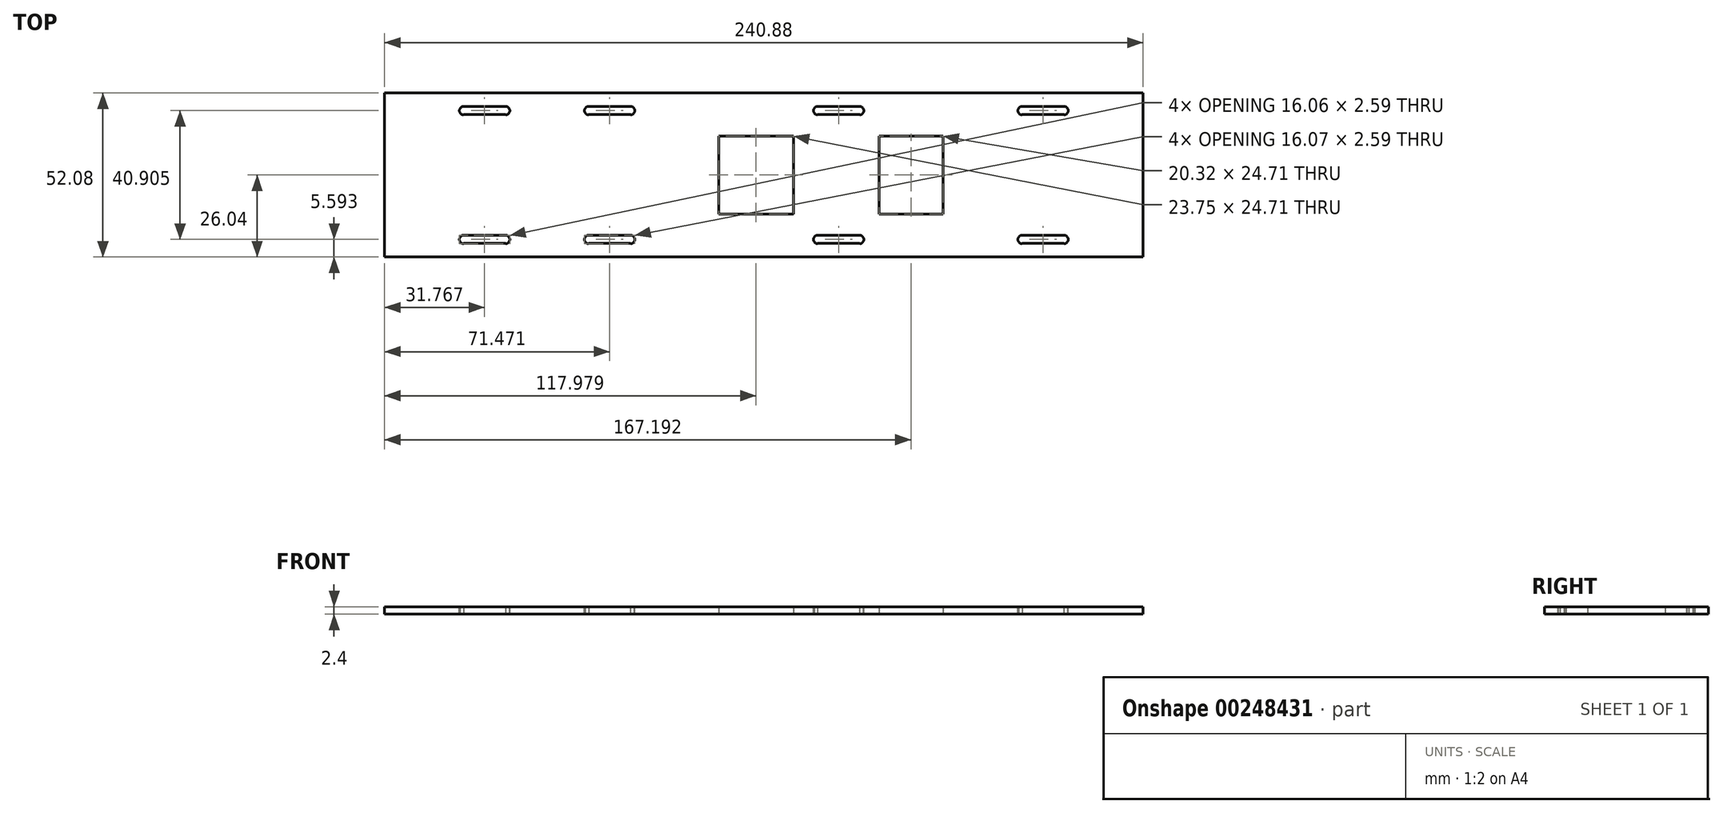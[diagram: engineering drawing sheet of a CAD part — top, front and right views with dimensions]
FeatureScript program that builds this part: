
annotation { "Feature Type Name" : "Feature", "Feature Type Description" : "" }
export const myFeature = defineFeature(function(context is Context, id is Id, definition is map)
    precondition{}
    {
        {
            var Q0;
            Q0=qCreatedBy(makeId("Top.planeOp"),FACE);
            var sketch = newSketch(context, id + "F0", { "sketchPlane" : qUnion([Q0])});
            skLineSegment(sketch, "E0", {"start": v(120.44, 26.04) * mm, "end": v(120.44, -26.04) * mm});
            skLineSegment(sketch, "E1", {"start": v(120.44, -26.04) * mm, "end": v(-120.44, -26.04) * mm});
            skLineSegment(sketch, "E2", {"start": v(-120.44, -26.04) * mm, "end": v(-120.44, 26.04) * mm});
            skLineSegment(sketch, "E3", {"start": v(-120.44, 26.04) * mm, "end": v(120.44, 26.04) * mm});
            skLineSegment(sketch, "E4", {"start": v(-95.34, -19.17) * mm, "end": v(-82.02, -19.17) * mm});
            skFitSpline(sketch, "E5", {"points": [v(-95.33, -19.17) * mm, v(-95.79, -19.17) * mm, v(-96.2, -19.41) * mm, v(-96.44, -19.8) * mm]});
            skFitSpline(sketch, "E6", {"points": [v(-96.44, -19.8) * mm, v(-96.67, -20.2) * mm, v(-96.67, -20.7) * mm, v(-96.44, -21.09) * mm]});
            skFitSpline(sketch, "E7", {"points": [v(-96.44, -21.09) * mm, v(-96.2, -21.48) * mm, v(-95.79, -21.72) * mm, v(-95.33, -21.72) * mm]});
            skFitSpline(sketch, "E8", {"points": [v(-82.02, -21.72) * mm, v(-81.56, -21.72) * mm, v(-81.14, -21.48) * mm, v(-80.9, -21.09) * mm]});
            skFitSpline(sketch, "E9", {"points": [v(-80.9, -21.09) * mm, v(-80.68, -20.7) * mm, v(-80.68, -20.2) * mm, v(-80.9, -19.8) * mm]});
            skFitSpline(sketch, "E10", {"points": [v(-80.9, -19.8) * mm, v(-81.14, -19.41) * mm, v(-81.56, -19.17) * mm, v(-82.02, -19.17) * mm]});
            skLineSegment(sketch, "E11", {"start": v(-82.02, -21.72) * mm, "end": v(-95.34, -21.72) * mm});
            skLineSegment(sketch, "E12", {"start": v(-55.64, -19.17) * mm, "end": v(-42.3, -19.17) * mm});
            skFitSpline(sketch, "E13", {"points": [v(-55.63, -19.17) * mm, v(-56.09, -19.17) * mm, v(-56.51, -19.41) * mm, v(-56.74, -19.8) * mm]});
            skFitSpline(sketch, "E14", {"points": [v(-56.74, -19.8) * mm, v(-56.97, -20.2) * mm, v(-56.97, -20.7) * mm, v(-56.74, -21.09) * mm]});
            skFitSpline(sketch, "E15", {"points": [v(-56.74, -21.09) * mm, v(-56.51, -21.48) * mm, v(-56.09, -21.72) * mm, v(-55.63, -21.72) * mm]});
            skFitSpline(sketch, "E16", {"points": [v(-42.3, -21.72) * mm, v(-41.85, -21.72) * mm, v(-41.43, -21.48) * mm, v(-41.2, -21.09) * mm]});
            skFitSpline(sketch, "E17", {"points": [v(-41.2, -21.09) * mm, v(-40.97, -20.7) * mm, v(-40.97, -20.2) * mm, v(-41.2, -19.8) * mm]});
            skFitSpline(sketch, "E18", {"points": [v(-41.2, -19.8) * mm, v(-41.43, -19.41) * mm, v(-41.85, -19.17) * mm, v(-42.3, -19.17) * mm]});
            skLineSegment(sketch, "E19", {"start": v(-42.3, -21.72) * mm, "end": v(-55.64, -21.72) * mm});
            skLineSegment(sketch, "E20", {"start": v(17.1, -19.17) * mm, "end": v(30.42, -19.17) * mm});
            skFitSpline(sketch, "E21", {"points": [v(17.1, -19.17) * mm, v(16.65, -19.17) * mm, v(16.23, -19.41) * mm, v(16, -19.8) * mm]});
            skFitSpline(sketch, "E22", {"points": [v(16, -19.8) * mm, v(15.77, -20.2) * mm, v(15.77, -20.7) * mm, v(16, -21.09) * mm]});
            skFitSpline(sketch, "E23", {"points": [v(16, -21.09) * mm, v(16.23, -21.48) * mm, v(16.65, -21.72) * mm, v(17.1, -21.72) * mm]});
            skFitSpline(sketch, "E24", {"points": [v(30.42, -21.72) * mm, v(30.88, -21.72) * mm, v(31.3, -21.48) * mm, v(31.53, -21.09) * mm]});
            skFitSpline(sketch, "E25", {"points": [v(31.53, -21.09) * mm, v(31.76, -20.7) * mm, v(31.76, -20.2) * mm, v(31.53, -19.8) * mm]});
            skFitSpline(sketch, "E26", {"points": [v(31.53, -19.8) * mm, v(31.3, -19.41) * mm, v(30.88, -19.17) * mm, v(30.42, -19.17) * mm]});
            skLineSegment(sketch, "E27", {"start": v(30.42, -21.72) * mm, "end": v(17.1, -21.72) * mm});
            skLineSegment(sketch, "E28", {"start": v(82.01, -19.17) * mm, "end": v(95.35, -19.17) * mm});
            skFitSpline(sketch, "E29", {"points": [v(82.03, -19.17) * mm, v(81.57, -19.17) * mm, v(81.15, -19.41) * mm, v(80.92, -19.8) * mm]});
            skFitSpline(sketch, "E30", {"points": [v(80.92, -19.8) * mm, v(80.69, -20.2) * mm, v(80.69, -20.7) * mm, v(80.92, -21.09) * mm]});
            skFitSpline(sketch, "E31", {"points": [v(80.92, -21.09) * mm, v(81.15, -21.48) * mm, v(81.57, -21.72) * mm, v(82.03, -21.72) * mm]});
            skFitSpline(sketch, "E32", {"points": [v(95.35, -21.72) * mm, v(95.8, -21.72) * mm, v(96.23, -21.48) * mm, v(96.46, -21.09) * mm]});
            skFitSpline(sketch, "E33", {"points": [v(96.46, -21.09) * mm, v(96.69, -20.7) * mm, v(96.69, -20.2) * mm, v(96.46, -19.8) * mm]});
            skFitSpline(sketch, "E34", {"points": [v(96.46, -19.8) * mm, v(96.23, -19.41) * mm, v(95.8, -19.17) * mm, v(95.35, -19.17) * mm]});
            skLineSegment(sketch, "E35", {"start": v(95.35, -21.72) * mm, "end": v(82.02, -21.72) * mm});
            skLineSegment(sketch, "E36", {"start": v(-14.34, -12.36) * mm, "end": v(-14.34, 12.36) * mm});
            skLineSegment(sketch, "E37", {"start": v(-14.34, 12.36) * mm, "end": v(9.41, 12.36) * mm});
            skLineSegment(sketch, "E38", {"start": v(9.41, 12.36) * mm, "end": v(9.41, -12.36) * mm});
            skLineSegment(sketch, "E39", {"start": v(9.41, -12.36) * mm, "end": v(-14.34, -12.36) * mm});
            skLineSegment(sketch, "E40", {"start": v(36.6, -12.36) * mm, "end": v(36.6, 12.36) * mm});
            skLineSegment(sketch, "E41", {"start": v(36.6, 12.36) * mm, "end": v(56.91, 12.36) * mm});
            skLineSegment(sketch, "E42", {"start": v(56.91, 12.36) * mm, "end": v(56.91, -12.36) * mm});
            skLineSegment(sketch, "E43", {"start": v(56.91, -12.36) * mm, "end": v(36.6, -12.36) * mm});
            skLineSegment(sketch, "E44", {"start": v(-95.34, 19.18) * mm, "end": v(-82.02, 19.18) * mm});
            skFitSpline(sketch, "E45", {"points": [v(-95.33, 21.73) * mm, v(-95.79, 21.74) * mm, v(-96.2, 21.5) * mm, v(-96.44, 21.1) * mm]});
            skFitSpline(sketch, "E46", {"points": [v(-96.44, 21.1) * mm, v(-96.67, 20.7) * mm, v(-96.67, 20.21) * mm, v(-96.44, 19.82) * mm]});
            skFitSpline(sketch, "E47", {"points": [v(-96.44, 19.82) * mm, v(-96.2, 19.42) * mm, v(-95.79, 19.18) * mm, v(-95.33, 19.18) * mm]});
            skFitSpline(sketch, "E48", {"points": [v(-82.02, 19.18) * mm, v(-81.56, 19.18) * mm, v(-81.14, 19.42) * mm, v(-80.9, 19.82) * mm]});
            skFitSpline(sketch, "E49", {"points": [v(-80.9, 19.82) * mm, v(-80.68, 20.21) * mm, v(-80.68, 20.7) * mm, v(-80.9, 21.1) * mm]});
            skFitSpline(sketch, "E50", {"points": [v(-80.9, 21.1) * mm, v(-81.14, 21.5) * mm, v(-81.56, 21.74) * mm, v(-82.02, 21.73) * mm]});
            skLineSegment(sketch, "E51", {"start": v(-82.02, 21.73) * mm, "end": v(-95.34, 21.73) * mm});
            skLineSegment(sketch, "E52", {"start": v(-55.64, 19.18) * mm, "end": v(-42.3, 19.18) * mm});
            skFitSpline(sketch, "E53", {"points": [v(-55.63, 21.73) * mm, v(-56.09, 21.74) * mm, v(-56.51, 21.5) * mm, v(-56.74, 21.1) * mm]});
            skFitSpline(sketch, "E54", {"points": [v(-56.74, 21.1) * mm, v(-56.97, 20.7) * mm, v(-56.97, 20.21) * mm, v(-56.74, 19.82) * mm]});
            skFitSpline(sketch, "E55", {"points": [v(-56.74, 19.82) * mm, v(-56.51, 19.42) * mm, v(-56.09, 19.18) * mm, v(-55.63, 19.18) * mm]});
            skFitSpline(sketch, "E56", {"points": [v(-42.3, 19.18) * mm, v(-41.85, 19.18) * mm, v(-41.43, 19.42) * mm, v(-41.2, 19.82) * mm]});
            skFitSpline(sketch, "E57", {"points": [v(-41.2, 19.82) * mm, v(-40.97, 20.21) * mm, v(-40.97, 20.7) * mm, v(-41.2, 21.1) * mm]});
            skFitSpline(sketch, "E58", {"points": [v(-41.2, 21.1) * mm, v(-41.43, 21.5) * mm, v(-41.85, 21.74) * mm, v(-42.3, 21.73) * mm]});
            skLineSegment(sketch, "E59", {"start": v(-42.3, 21.73) * mm, "end": v(-55.64, 21.73) * mm});
            skLineSegment(sketch, "E60", {"start": v(17.1, 19.18) * mm, "end": v(30.42, 19.18) * mm});
            skFitSpline(sketch, "E61", {"points": [v(17.1, 21.73) * mm, v(16.65, 21.74) * mm, v(16.23, 21.5) * mm, v(16, 21.1) * mm]});
            skFitSpline(sketch, "E62", {"points": [v(16, 21.1) * mm, v(15.77, 20.7) * mm, v(15.77, 20.21) * mm, v(16, 19.82) * mm]});
            skFitSpline(sketch, "E63", {"points": [v(16, 19.82) * mm, v(16.23, 19.42) * mm, v(16.65, 19.18) * mm, v(17.1, 19.18) * mm]});
            skFitSpline(sketch, "E64", {"points": [v(30.42, 19.18) * mm, v(30.88, 19.18) * mm, v(31.3, 19.42) * mm, v(31.53, 19.82) * mm]});
            skFitSpline(sketch, "E65", {"points": [v(31.53, 19.82) * mm, v(31.76, 20.21) * mm, v(31.76, 20.7) * mm, v(31.53, 21.1) * mm]});
            skFitSpline(sketch, "E66", {"points": [v(31.53, 21.1) * mm, v(31.3, 21.5) * mm, v(30.88, 21.74) * mm, v(30.42, 21.73) * mm]});
            skLineSegment(sketch, "E67", {"start": v(30.42, 21.73) * mm, "end": v(17.1, 21.73) * mm});
            skLineSegment(sketch, "E68", {"start": v(82.02, 19.18) * mm, "end": v(95.35, 19.18) * mm});
            skFitSpline(sketch, "E69", {"points": [v(82.03, 21.73) * mm, v(81.57, 21.74) * mm, v(81.15, 21.5) * mm, v(80.92, 21.1) * mm]});
            skFitSpline(sketch, "E70", {"points": [v(80.92, 21.1) * mm, v(80.69, 20.7) * mm, v(80.69, 20.21) * mm, v(80.92, 19.82) * mm]});
            skFitSpline(sketch, "E71", {"points": [v(80.92, 19.82) * mm, v(81.15, 19.42) * mm, v(81.57, 19.18) * mm, v(82.03, 19.18) * mm]});
            skFitSpline(sketch, "E72", {"points": [v(95.35, 19.18) * mm, v(95.8, 19.18) * mm, v(96.23, 19.42) * mm, v(96.46, 19.82) * mm]});
            skFitSpline(sketch, "E73", {"points": [v(96.46, 19.82) * mm, v(96.69, 20.21) * mm, v(96.69, 20.7) * mm, v(96.46, 21.1) * mm]});
            skFitSpline(sketch, "E74", {"points": [v(96.46, 21.1) * mm, v(96.23, 21.5) * mm, v(95.8, 21.74) * mm, v(95.35, 21.73) * mm]});
            skLineSegment(sketch, "E75", {"start": v(95.35, 21.73) * mm, "end": v(82.01, 21.73) * mm});
            skSolve(sketch);
        }
        {
            var Q0;
            Q0 = qSketchRegion(id + "F0", true);
            extrude(context, id + "F1", {"entities" : qUnion([Q0]), "depth" : 2.4 * mm});
        }
    });
